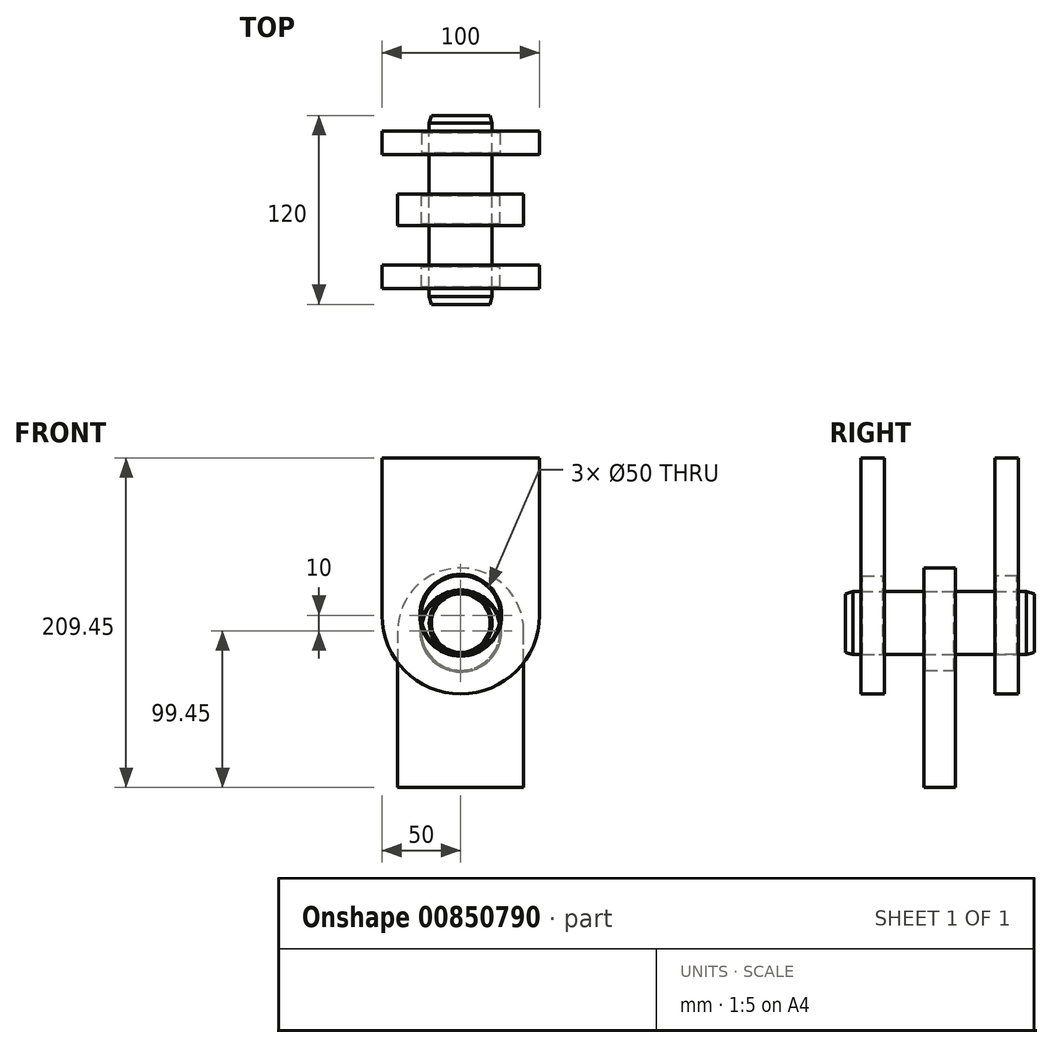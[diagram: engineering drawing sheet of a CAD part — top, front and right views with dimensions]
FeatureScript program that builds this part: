
annotation { "Feature Type Name" : "Feature", "Feature Type Description" : "" }
export const myFeature = defineFeature(function(context is Context, id is Id, definition is map)
    precondition{}
    {
        {
            var Q0;
            Q0=qCreatedBy(makeId("Front.planeOp"),FACE);
            var sketch = newSketch(context, id + "F0", { "sketchPlane" : qUnion([Q0])});
            skArc(sketch, "E0", {"start": v(-50, 0) * mm, "mid": v(0, -50) * mm, "end": v(50, 0) * mm});
            skCircle(sketch, "E1", {"center": v(0, 0) * mm, "radius": 25 * mm});
            skLineSegment(sketch, "E2", {"start": v(-50, 0) * mm, "end": v(-50, 100) * mm});
            skLineSegment(sketch, "E3", {"start": v(-50, 100) * mm, "end": v(50, 100) * mm});
            skLineSegment(sketch, "E4", {"start": v(50, 100) * mm, "end": v(50, 0) * mm});
            skSolve(sketch);
        }
        {
            var Q0;
            Q0=makeQuery(id+"F0.imprint","IMPRINT",FACE,{"disambiguationData":[TD([[makeQuery(id+"F0.imprint","IMPRINT",EDGE,{"derivedFrom":sQuery(id+"F0.wireOp",EDGE,"E0")}),1.0]])]});
            extrude(context, id + "F1", {"entities" : qUnion([Q0]), "depth" : 50 * mm, "offsetDistance" : 25 * mm, "hasSecondDirection" : true, "secondDirectionOppositeDirection" : false, "secondDirectionDepth" : 35 * mm});
        }
        {
            var Q0;
            Q0=makeQuery(id+"F1.opExtrude","CAP_EDGE",EDGE,{"disambiguationData":[OSD([sQuery(id+"F0.wireOp",EDGE,"E1")])],"isStart":false});
            var Q1;
            Q1=makeQuery(id+"F1.opExtrude","CAP_EDGE",EDGE,{"disambiguationData":[OSD([sQuery(id+"F0.wireOp",EDGE,"E1")])],"isStart":true});
            chamfer(context, id + "F2", {"entities" : qUnion([Q0, Q1]), "width" : 1 * mm, "tangentPropagation" : true});
        }
        {
            var Q0;
            Q0=qCreatedBy(makeId("Front.planeOp"),FACE);
            var sketch = newSketch(context, id + "F3", { "sketchPlane" : qUnion([Q0])});
            skArc(sketch, "E5", {"start": v(40, -10) * mm, "mid": v(0, 30) * mm, "end": v(-40, -10) * mm});
            skLineSegment(sketch, "E6", {"start": v(-40, -10) * mm, "end": v(-40, -109.45) * mm});
            skLineSegment(sketch, "E7", {"start": v(-40, -109.45) * mm, "end": v(40, -109.45) * mm});
            skLineSegment(sketch, "E8", {"start": v(40, -109.45) * mm, "end": v(40, -10) * mm});
            skCircle(sketch, "E9", {"center": v(0, -10) * mm, "radius": 25 * mm});
            skSolve(sketch);
        }
        {
            var Q0;
            Q0=makeQuery(id+"F3.imprint","IMPRINT",FACE,{"disambiguationData":[TD([[makeQuery(id+"F3.imprint","IMPRINT",EDGE,{"derivedFrom":sQuery(id+"F3.wireOp",EDGE,"E5")}),1.0]])]});
            extrude(context, id + "F4", {"entities" : qUnion([Q0]), "endBound" : BoundingType.SYMMETRIC, "depth" : 20 * mm, "offsetDistance" : 25 * mm});
        }
        {
            var Q0;
            Q0=makeQuery(id+"F4.opExtrude","SWEPT_FACE",FACE,{"disambiguationData":[OSD([sQuery(id+"F3.wireOp",EDGE,"E9")])]});
            chamfer(context, id + "F5", {"entities" : qUnion([Q0]), "width" : 1 * mm, "tangentPropagation" : true});
        }
        {
            var Q0;
            Q0=makeQuery(id+"F1.opExtrude","SWEPT_BODY",BODY,{"disambiguationData":[OSD([sQuery(id+"F0.wireOp",EDGE,"E0"),sQuery(id+"F0.wireOp",EDGE,"E1"),sQuery(id+"F0.wireOp",EDGE,"E2"),sQuery(id+"F0.wireOp",EDGE,"E3"),sQuery(id+"F0.wireOp",EDGE,"E4")])]});
            var Q1;
            Q1=qCreatedBy(makeId("Front.planeOp"),FACE);
            mirror(context, id + "F6", {"entities" : qUnion([Q0]), "mirrorPlane" : qUnion([Q1])});
        }
        {
            var Q0;
            Q0=qCreatedBy(makeId("Front.planeOp"),FACE);
            var sketch = newSketch(context, id + "F7", { "sketchPlane" : qUnion([Q0])});
            skCircle(sketch, "E10", {"center": v(0, -5) * mm, "radius": 20 * mm});
            skSolve(sketch);
        }
        {
            var Q0;
            Q0 = qSketchRegion(id + "F7", true);
            extrude(context, id + "F8", {"entities" : qUnion([Q0]), "endBound" : BoundingType.SYMMETRIC, "depth" : 120 * mm, "offsetDistance" : 25 * mm});
        }
        {
            var Q0;
            Q0=makeQuery(id+"F8.opExtrude","CAP_EDGE",EDGE,{"disambiguationData":[OSD([sQuery(id+"F7.wireOp",EDGE,"E10")])],"isStart":false});
            var Q1;
            Q1=makeQuery(id+"F8.opExtrude","CAP_EDGE",EDGE,{"disambiguationData":[OSD([sQuery(id+"F7.wireOp",EDGE,"E10")])],"isStart":true});
            chamfer(context, id + "F9", {"entities" : qUnion([Q0, Q1]), "chamferType" : ChamferType.OFFSET_ANGLE, "width" : 5 * mm, "oppositeDirection" : true, "angle" : 15 * degree, "tangentPropagation" : true});
        }
    });
